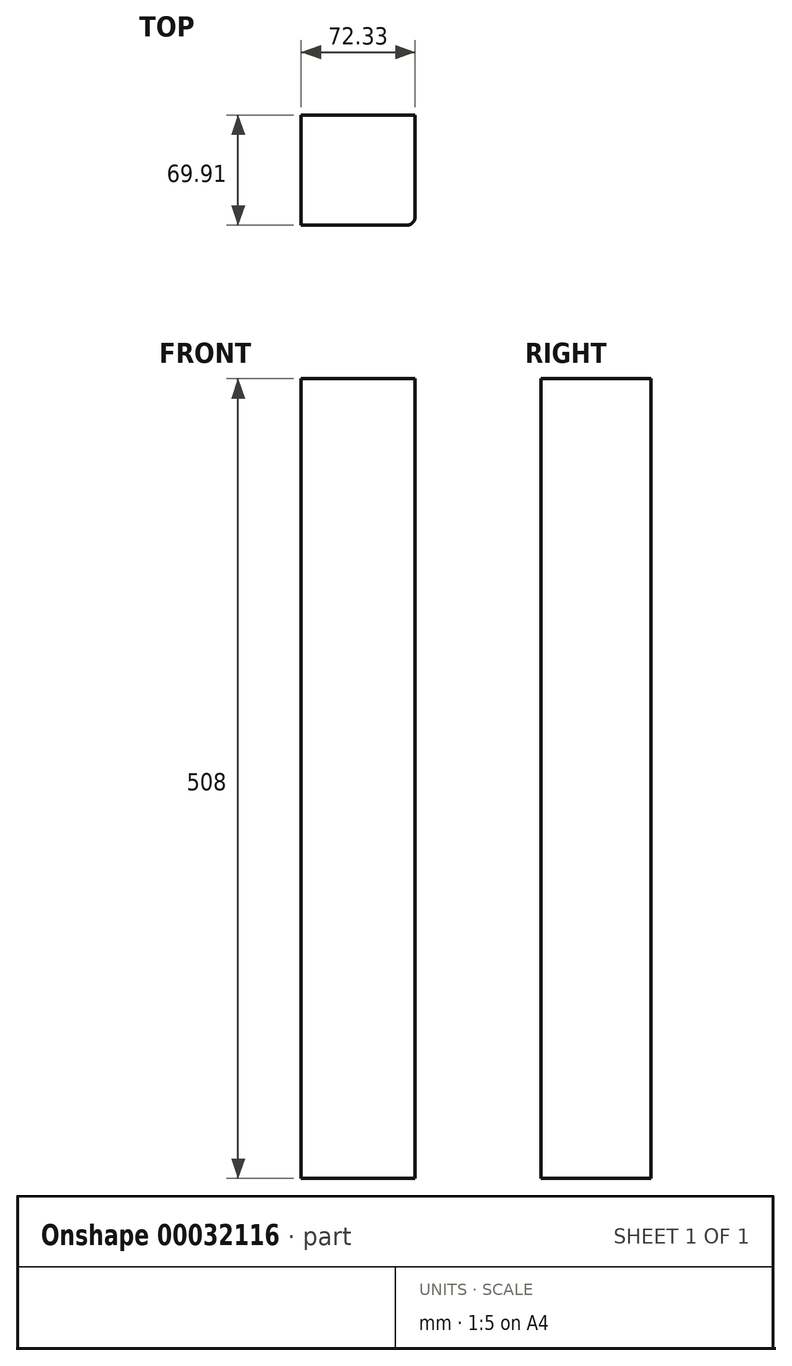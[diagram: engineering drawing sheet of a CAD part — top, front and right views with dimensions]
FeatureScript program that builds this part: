
annotation { "Feature Type Name" : "Feature", "Feature Type Description" : "" }
export const myFeature = defineFeature(function(context is Context, id is Id, definition is map)
    precondition{}
    {
        {
            var Q0;
            Q0=qCreatedBy(makeId("Top.planeOp"),FACE);
            var sketch = newSketch(context, id + "F0", { "sketchPlane" : qUnion([Q0])});
            skLineSegment(sketch, "E0.bottom", {"start": v(0, 0) * mm, "end": v(72.33, 0) * mm});
            skLineSegment(sketch, "E0.top", {"start": v(0, -69.9) * mm, "end": v(72.33, -69.9) * mm});
            skLineSegment(sketch, "E0.left", {"start": v(0, 0) * mm, "end": v(0, -69.9) * mm});
            skLineSegment(sketch, "E0.right", {"start": v(72.33, 0) * mm, "end": v(72.33, -69.9) * mm});
            skSolve(sketch);
        }
        {
            var Q0;
            Q0 = qSketchRegion(id + "F0", true);
            extrude(context, id + "F1", {"entities" : qUnion([Q0]), "depth" : 508 * mm});
        }
        {
            var Q0;
            Q0=makeQuery(id+"F1.opExtrude","SWEPT_EDGE",EDGE,{"disambiguationData":[OSD([sQuery(id+"F0.wireOp",EDGE,"E0.top"),sQuery(id+"F0.wireOp",EDGE,"E0.right")])]});
            fillet(context, id + "F2", {"entities" : qUnion([Q0]), "radius" : 5.08 * mm, "tangentPropagation" : true, "allowEdgeOverflow" : false});
        }
    });
